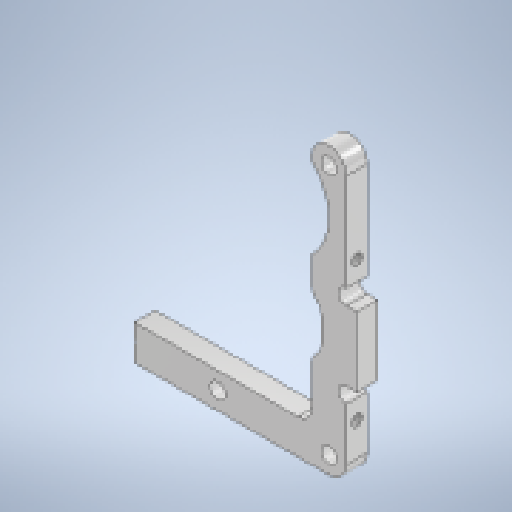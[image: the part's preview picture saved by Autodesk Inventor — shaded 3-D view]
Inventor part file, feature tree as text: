
AUTODESK INVENTOR PART (.ipt)
format: ipt  version: 2025.1 (Build 291241000, 241)  size: 251,904 bytes
history: native  units: mm
features: reference x11, other x6, sketch x3, fillet x2, hole x2, extrude x1
ambient origin geometry x8: Origin, YZ Plane, XZ Plane, XY Plane, X Axis, Y Axis, Z Axis, Center Point
bodies: Body1 (feature_tree)
feature tree (25):
  other  "ソリッド1"
  extrude  "押し出し1"  Depth=2.2mm
  fillet  "フィレット1"  Radius=2.2mm
  hole  "穴1"  [1 undecoded]
  hole  "穴2"  [1 undecoded]
  fillet  "フィレット2"  Radius=2.2mm
  sketch  "スケッチ1"
  reference  "参照1"
  reference  "参照2"
  reference  "参照3"
  reference  "参照4"
  reference  "参照5"
  reference  "参照6"
  reference  "参照7"
  reference  "参照8"
  reference  "参照9"
  sketch  "スケッチ2"
  reference  "参照10"
  reference  "参照11"
  sketch  "スケッチ3"
  other  "<userpath>\Documents\Inventor\Vixen\doutai.iam"
  other  "doutai.iam"
  other  "KRS2500_scale:8"
  other  "KSHI:1"
  other  "KRS2500_scale:1"
note: 2 required parameter values undecoded (feature->parameter linkage not recoverable at this tier; creation-order binding heuristic only, values carry confidence <= 0.55)
